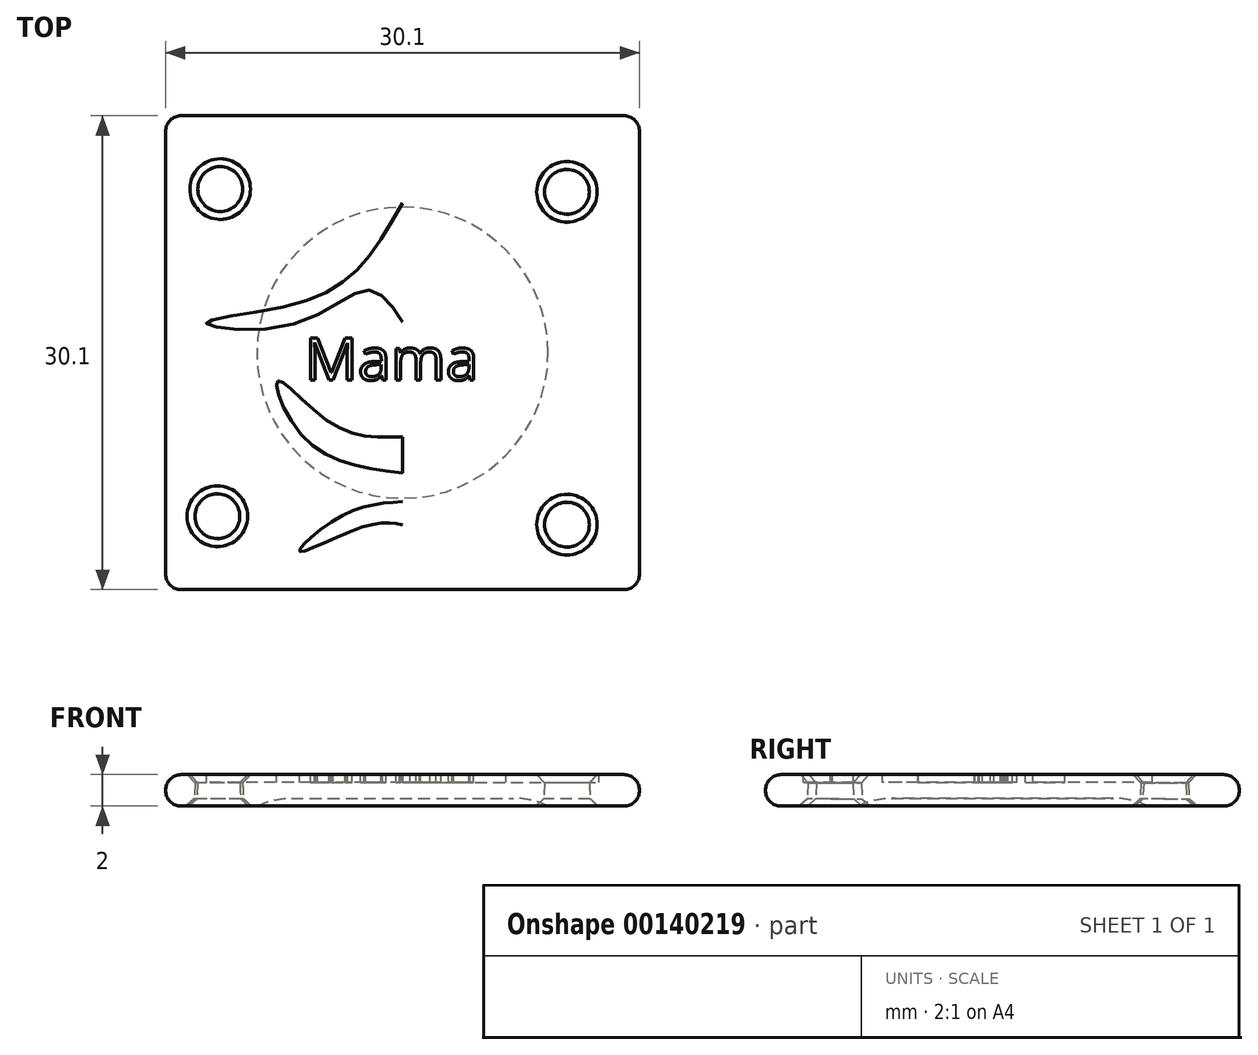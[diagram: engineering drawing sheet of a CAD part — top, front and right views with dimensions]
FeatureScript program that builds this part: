
annotation { "Feature Type Name" : "Feature", "Feature Type Description" : "" }
export const myFeature = defineFeature(function(context is Context, id is Id, definition is map)
    precondition{}
    {
        {
            var Q0;
            Q0=qCreatedBy(makeId("Top.planeOp"),FACE);
            var sketch = newSketch(context, id + "F0", { "sketchPlane" : qUnion([Q0])});
            skLineSegment(sketch, "E0.bottom", {"start": v(15, 15) * mm, "end": v(-15, 15) * mm});
            skLineSegment(sketch, "E0.top", {"start": v(15, -15) * mm, "end": v(-15, -15) * mm});
            skLineSegment(sketch, "E0.left", {"start": v(15, 15) * mm, "end": v(15, -15) * mm});
            skLineSegment(sketch, "E0.right", {"start": v(-15, 15) * mm, "end": v(-15, -15) * mm});
            skPoint(sketch, "E0.middle", {"position": v(0, 0) * mm});
            skCircle(sketch, "E1", {"center": v(10.44, 10.22) * mm, "radius": 1.5 * mm});
            skCircle(sketch, "E2", {"center": v(-11.58, 10.4) * mm, "radius": 1.5 * mm});
            skCircle(sketch, "E3", {"center": v(-11.76, -10.39) * mm, "radius": 1.5 * mm});
            skCircle(sketch, "E4", {"center": v(10.44, -10.92) * mm, "radius": 1.5 * mm});
            skSolve(sketch);
        }
        {
            var Q0;
            Q0=makeQuery(id+"F0.imprint","IMPRINT",FACE,{"disambiguationData":[TD([[makeQuery(id+"F0.imprint","IMPRINT",EDGE,{"derivedFrom":sQuery(id+"F0.wireOp",EDGE,"E0.bottom")}),1.0]])]});
            extrude(context, id + "F1", {"entities" : qUnion([Q0]), "depth" : 2 * mm, "hasDraft" : true, "draftAngle" : 3 * degree});
        }
        {
            var Q0;
            Q0=makeQuery(id+"F1.opExtrude","CAP_EDGE",EDGE,{"disambiguationData":[OSD([sQuery(id+"F0.wireOp",EDGE,"E0.top")])],"isStart":false});
            var Q1;
            Q1=makeQuery(id+"F1.opExtrude","CAP_EDGE",EDGE,{"disambiguationData":[OSD([sQuery(id+"F0.wireOp",EDGE,"E0.top")])],"isStart":true});
            var Q2;
            Q2=makeQuery(id+"F1.opExtrude","CAP_EDGE",EDGE,{"disambiguationData":[OSD([sQuery(id+"F0.wireOp",EDGE,"E0.right")])],"isStart":true});
            var Q3;
            Q3=makeQuery(id+"F1.opExtrude","CAP_EDGE",EDGE,{"disambiguationData":[OSD([sQuery(id+"F0.wireOp",EDGE,"E0.right")])],"isStart":false});
            var Q4;
            Q4=makeQuery(id+"F1.opExtrude","CAP_EDGE",EDGE,{"disambiguationData":[OSD([sQuery(id+"F0.wireOp",EDGE,"E0.left")])],"isStart":false});
            var Q5;
            Q5=makeQuery(id+"F1.opExtrude","CAP_EDGE",EDGE,{"disambiguationData":[OSD([sQuery(id+"F0.wireOp",EDGE,"E0.bottom")])],"isStart":false});
            var Q6;
            Q6=makeQuery(id+"F1.opExtrude","CAP_EDGE",EDGE,{"disambiguationData":[OSD([sQuery(id+"F0.wireOp",EDGE,"E0.bottom")])],"isStart":true});
            var Q7;
            Q7=makeQuery(id+"F1.opExtrude","CAP_EDGE",EDGE,{"disambiguationData":[OSD([sQuery(id+"F0.wireOp",EDGE,"E0.left")])],"isStart":true});
            var Q8;
            Q8=makeQuery(id+"F1.opExtrude","SWEPT_EDGE",EDGE,{"disambiguationData":[OSD([sQuery(id+"F0.wireOp",EDGE,"E0.top"),sQuery(id+"F0.wireOp",EDGE,"E0.right")])]});
            var Q9;
            Q9=makeQuery(id+"F1.opExtrude","SWEPT_EDGE",EDGE,{"disambiguationData":[OSD([sQuery(id+"F0.wireOp",EDGE,"E0.top"),sQuery(id+"F0.wireOp",EDGE,"E0.left")])]});
            var Q10;
            Q10=makeQuery(id+"F1.opExtrude","SWEPT_EDGE",EDGE,{"disambiguationData":[OSD([sQuery(id+"F0.wireOp",EDGE,"E0.bottom"),sQuery(id+"F0.wireOp",EDGE,"E0.right")])]});
            var Q11;
            Q11=makeQuery(id+"F1.opExtrude","SWEPT_EDGE",EDGE,{"disambiguationData":[OSD([sQuery(id+"F0.wireOp",EDGE,"E0.bottom"),sQuery(id+"F0.wireOp",EDGE,"E0.left")])]});
            fillet(context, id + "F2", {"entities" : qUnion([Q0, Q1, Q2, Q3, Q4, Q5, Q6, Q7, Q8, Q9, Q10, Q11]), "radius" : 1 * mm, "tangentPropagation" : true, "allowEdgeOverflow" : false});
        }
        {
            var Q0;
            Q0=makeQuery(id+"F1.opExtrude","CAP_EDGE",EDGE,{"disambiguationData":[OSD([sQuery(id+"F0.wireOp",EDGE,"E2")])],"isStart":false});
            var Q1;
            Q1=makeQuery(id+"F1.opExtrude","CAP_EDGE",EDGE,{"disambiguationData":[OSD([sQuery(id+"F0.wireOp",EDGE,"E1")])],"isStart":false});
            var Q2;
            Q2=makeQuery(id+"F1.opExtrude","CAP_EDGE",EDGE,{"disambiguationData":[OSD([sQuery(id+"F0.wireOp",EDGE,"E4")])],"isStart":false});
            var Q3;
            Q3=makeQuery(id+"F1.opExtrude","CAP_EDGE",EDGE,{"disambiguationData":[OSD([sQuery(id+"F0.wireOp",EDGE,"E3")])],"isStart":false});
            var Q4;
            Q4=makeQuery(id+"F1.opExtrude","CAP_EDGE",EDGE,{"disambiguationData":[OSD([sQuery(id+"F0.wireOp",EDGE,"E1")])],"isStart":true});
            var Q5;
            Q5=makeQuery(id+"F1.opExtrude","CAP_EDGE",EDGE,{"disambiguationData":[OSD([sQuery(id+"F0.wireOp",EDGE,"E2")])],"isStart":true});
            var Q6;
            Q6=makeQuery(id+"F1.opExtrude","CAP_EDGE",EDGE,{"disambiguationData":[OSD([sQuery(id+"F0.wireOp",EDGE,"E3")])],"isStart":true});
            var Q7;
            Q7=makeQuery(id+"F1.opExtrude","CAP_EDGE",EDGE,{"disambiguationData":[OSD([sQuery(id+"F0.wireOp",EDGE,"E4")])],"isStart":true});
            chamfer(context, id + "F3", {"entities" : qUnion([Q0, Q1, Q2, Q3, Q4, Q5, Q6, Q7]), "width" : 0.5 * mm, "tangentPropagation" : true});
        }
        {
            var Q0;
            Q0=makeQuery(id+"F1.opExtrude","CAP_FACE",FACE,{"disambiguationData":[OSD([sQuery(id+"F0.wireOp",EDGE,"E0.bottom"),sQuery(id+"F0.wireOp",EDGE,"E0.top"),sQuery(id+"F0.wireOp",EDGE,"E0.left"),sQuery(id+"F0.wireOp",EDGE,"E0.right"),sQuery(id+"F0.wireOp",EDGE,"E1"),sQuery(id+"F0.wireOp",EDGE,"E2"),sQuery(id+"F0.wireOp",EDGE,"E3"),sQuery(id+"F0.wireOp",EDGE,"E4")])],"isStart":false});
            var sketch = newSketch(context, id + "F4", { "sketchPlane" : qUnion([Q0])});
            skLineSegment(sketch, "E5", {"start": v(0, 21.2) * mm, "end": v(0, -20.45) * mm});
            skFitSpline(sketch, "E6", {"points": [v(0, 9.51) * mm, v(-2.85, 5.31) * mm, v(-7.44, 2.93) * mm, v(-12.46, 1.9) * mm, v(-6.96, 1.8) * mm, v(-2.11, 3.97) * mm, v(0, 1.93) * mm], "startDerivative": vector(-15.32, -26.84) * mm, "endDerivative": vector(14.79, -22.8) * mm});
            skFitSpline(sketch, "E7", {"points": [v(0, 12.63) * mm, v(-3.63, 11.16) * mm, v(-5.8, 8.95) * mm, v(-6.92, 5.87) * mm], "startDerivative": vector(-10.88, -3.5) * mm, "endDerivative": vector(-2.75, -9.9) * mm});
            skFitSpline(sketch, "E8", {"points": [v(-6.92, 5.87) * mm, v(-3.93, 8.56) * mm, v(0, 9.51) * mm], "startDerivative": vector(5.52, 6.25) * mm, "endDerivative": vector(8.32, 1.03) * mm});
            skFitSpline(sketch, "E9", {"points": [v(0, -5.34) * mm, v(-4.54, -4.48) * mm, v(-7.92, -1.8) * mm, v(-6.27, -5.38) * mm, v(0, -7.64) * mm], "startDerivative": vector(-18.38, -0.72) * mm, "endDerivative": vector(23.98, -2.93) * mm});
            skFitSpline(sketch, "E10", {"points": [v(0, -9.45) * mm, v(-3.93, -10.4) * mm, v(-6.53, -12.62) * mm, v(-2.35, -11.01) * mm, v(0, -10.93) * mm], "startDerivative": vector(-13.97, -0.92) * mm, "endDerivative": vector(9.15, -1.81) * mm});
            skFitSpline(sketch, "E11.MirrorCS", {"points": [v(0, 9.51) * mm, v(2.85, 5.31) * mm, v(7.44, 2.93) * mm, v(12.46, 1.9) * mm, v(6.96, 1.8) * mm, v(2.11, 3.97) * mm, v(0, 1.93) * mm], "startDerivative": vector(15.32, -26.84) * mm, "endDerivative": vector(-14.79, -22.8) * mm});
            skFitSpline(sketch, "E12.MirrorCS", {"points": [v(0, -5.34) * mm, v(4.54, -4.48) * mm, v(7.92, -1.8) * mm, v(6.27, -5.38) * mm, v(0, -7.64) * mm], "startDerivative": vector(18.38, -0.72) * mm, "endDerivative": vector(-23.98, -2.93) * mm});
            skFitSpline(sketch, "E13.MirrorCS", {"points": [v(0, -5.34) * mm, v(4.54, -4.48) * mm, v(7.92, -1.8) * mm, v(6.27, -5.38) * mm, v(0, -7.64) * mm], "startDerivative": vector(18.38, -0.72) * mm, "endDerivative": vector(-23.98, -2.93) * mm});
            skFitSpline(sketch, "E14.MirrorCS", {"points": [v(0, -9.45) * mm, v(3.93, -10.4) * mm, v(6.53, -12.62) * mm, v(2.35, -11.01) * mm, v(0, -10.93) * mm], "startDerivative": vector(13.97, -0.92) * mm, "endDerivative": vector(-9.15, -1.81) * mm});
            skFitSpline(sketch, "E15.MirrorCS", {"points": [v(0, 12.63) * mm, v(3.63, 11.16) * mm, v(5.8, 8.95) * mm, v(6.92, 5.87) * mm], "startDerivative": vector(10.88, -3.5) * mm, "endDerivative": vector(2.75, -9.9) * mm});
            skFitSpline(sketch, "E16.MirrorCS", {"points": [v(0, 12.63) * mm, v(3.63, 11.16) * mm, v(5.8, 8.95) * mm, v(6.92, 5.87) * mm], "startDerivative": vector(10.88, -3.5) * mm, "endDerivative": vector(2.75, -9.9) * mm});
            skFitSpline(sketch, "E17.MirrorCS", {"points": [v(6.92, 5.87) * mm, v(3.93, 8.56) * mm, v(0, 9.51) * mm], "startDerivative": vector(-5.52, 6.25) * mm, "endDerivative": vector(-8.32, 1.03) * mm});
            skText(sketch, "E18", { "text": "Mama", "fontName": "OpenSans-Regular.ttf"});
            const initialGuessF4  = {"E18": [-0.00622, -0.00174, 1, 0, 0.0027]};
            skSetInitialGuess(sketch, initialGuessF4);
            skSolve(sketch);
        }
        {
            var Q0;
            Q0=makeQuery(id+"F4.imprint","IMPRINT",FACE,{"disambiguationData":[TD([[makeQuery(id+"F4.imprint","IMPRINT",EDGE,{"derivedFrom":sQuery(id+"F4.wireOp",EDGE,"E18.sketch_text.stroke-0")}),-1.0]])]});
            var Q1;
            Q1=makeQuery(id+"F4.imprint","IMPRINT",FACE,{"disambiguationData":[TD([[makeQuery(id+"F4.imprint","IMPRINT",EDGE,{"derivedFrom":sQuery(id+"F4.wireOp",EDGE,"E18.sketch_text.stroke-18")}),-1.0]])]});
            var Q2;
            {var subQ0=sQuery(id+"F4.wireOp",EDGE,"E18.sketch_text.stroke-56");Q2=makeQuery(id+"F4.imprint","IMPRINT",FACE,{"disambiguationData":[TD([[makeQuery(id+"F4.imprint","IMPRINT",EDGE,{"derivedFrom":subQ0}),-1.0]])]});}
            var Q3;
            Q3=makeQuery(id+"F4.imprint","IMPRINT",FACE,{"disambiguationData":[TD([[makeQuery(id+"F4.imprint","IMPRINT",EDGE,{"derivedFrom":sQuery(id+"F4.wireOp",EDGE,"E18.sketch_text.stroke-45")}),-1.0]])]});
            var Q4;
            Q4=makeQuery(id+"F4.imprint","IMPRINT",FACE,{"disambiguationData":[TD([[makeQuery(id+"F4.imprint","IMPRINT",EDGE,{"derivedFrom":sQuery(id+"F4.wireOp",EDGE,"E18.sketch_text.stroke-73")}),-1.0]])]});
            var Q5;
            {var subQ1=sQuery(id+"F4.wireOp",EDGE,"E6");Q5=makeQuery(id+"F4.imprint","IMPRINT",FACE,{"disambiguationData":[TD([[makeQuery(id+"F4.imprint","IMPRINT",EDGE,{"derivedFrom":subQ1}),1.0]])]});}
            var Q6;
            {var subQ0=sQuery(id+"F4.wireOp",EDGE,"E11.MirrorCS");Q6=makeQuery(id+"F4.imprint","IMPRINT",FACE,{"disambiguationData":[TD([[makeQuery(id+"F4.imprint","IMPRINT",EDGE,{"derivedFrom":subQ0}),-1.0]])]});}
            var Q7;
            {var subQ0=sQuery(id+"F4.wireOp",EDGE,"E13.MirrorCS");Q7=makeQuery(id+"F4.imprint","IMPRINT",FACE,{"disambiguationData":[TD([[makeQuery(id+"F4.imprint","IMPRINT",EDGE,{"derivedFrom":subQ0}),-1.0]])]});}
            var Q8;
            {var subQ1=sQuery(id+"F4.wireOp",EDGE,"E9");Q8=makeQuery(id+"F4.imprint","IMPRINT",FACE,{"disambiguationData":[TD([[makeQuery(id+"F4.imprint","IMPRINT",EDGE,{"derivedFrom":subQ1}),1.0]])]});}
            var Q9;
            {var subQ1=sQuery(id+"F4.wireOp",EDGE,"E10");Q9=makeQuery(id+"F4.imprint","IMPRINT",FACE,{"disambiguationData":[TD([[makeQuery(id+"F4.imprint","IMPRINT",EDGE,{"derivedFrom":subQ1}),1.0]])]});}
            var Q10;
            {var subQ0=sQuery(id+"F4.wireOp",EDGE,"E14.MirrorCS");Q10=makeQuery(id+"F4.imprint","IMPRINT",FACE,{"disambiguationData":[TD([[makeQuery(id+"F4.imprint","IMPRINT",EDGE,{"derivedFrom":subQ0}),-1.0]])]});}
            extrude(context, id + "F5", {"entities" : qUnion([Q0, Q1, Q2, Q3, Q4, Q5, Q6, Q7, Q8, Q9, Q10]), "operationType" : NewBodyOperationType.REMOVE, "oppositeDirection" : true, "depth" : 0.5 * mm});
        }
        {
            var Q0;
            Q0=makeQuery(id+"F1.opExtrude","CAP_FACE",FACE,{"disambiguationData":[OSD([sQuery(id+"F0.wireOp",EDGE,"E0.bottom"),sQuery(id+"F0.wireOp",EDGE,"E0.top"),sQuery(id+"F0.wireOp",EDGE,"E0.left"),sQuery(id+"F0.wireOp",EDGE,"E0.right"),sQuery(id+"F0.wireOp",EDGE,"E1"),sQuery(id+"F0.wireOp",EDGE,"E2"),sQuery(id+"F0.wireOp",EDGE,"E3"),sQuery(id+"F0.wireOp",EDGE,"E4")])],"isStart":true});
            var sketch = newSketch(context, id + "F6", { "sketchPlane" : qUnion([Q0])});
            skCircle(sketch, "E19", {"center": v(0, 0) * mm, "radius": 9.25 * mm});
            skSolve(sketch);
        }
        {
            var Q0;
            Q0=makeQuery(id+"F6.imprint","IMPRINT",FACE,{"disambiguationData":[TD([[makeQuery(id+"F6.imprint","IMPRINT",EDGE,{"derivedFrom":sQuery(id+"F6.wireOp",EDGE,"E19")}),1.0]])]});
            extrude(context, id + "F7", {"entities" : qUnion([Q0]), "operationType" : NewBodyOperationType.REMOVE, "oppositeDirection" : true, "depth" : 0.5 * mm});
        }
        {
            var Q0;
            Q0=makeQuery(id+"F7.boolean.opBoolean","COPY",EDGE,{"derivedFrom":makeQuery(id+"F7.opExtrude","CAP_EDGE",EDGE,{"disambiguationData":[OSD([sQuery(id+"F6.wireOp",EDGE,"E19")])],"isStart":false})});
            fillet(context, id + "F8", {"entities" : qUnion([Q0]), "radius" : 5.08 * mm, "tangentPropagation" : true, "allowEdgeOverflow" : false});
        }
    });
